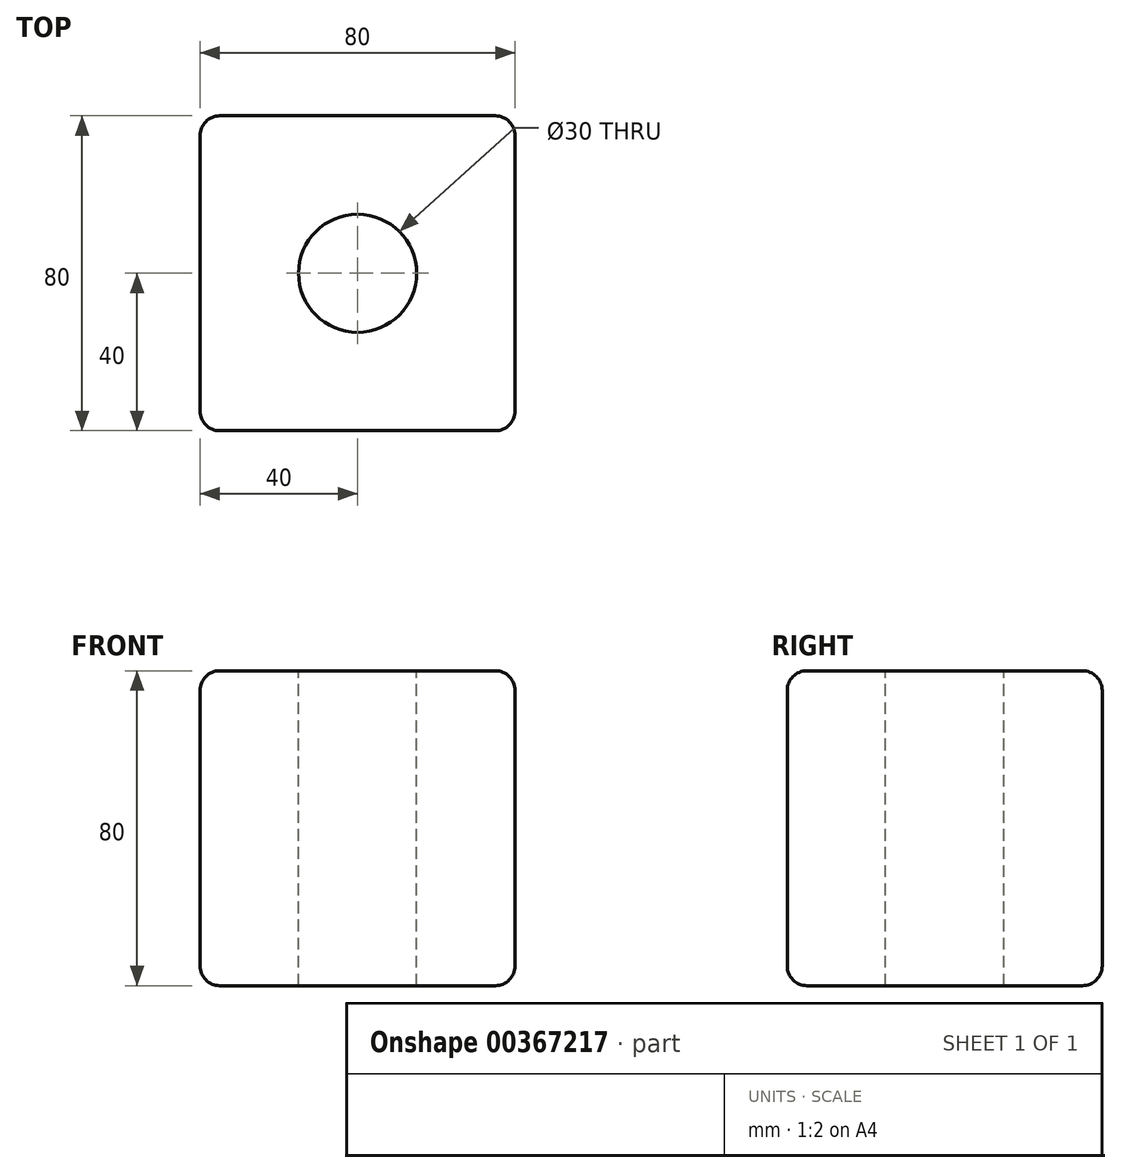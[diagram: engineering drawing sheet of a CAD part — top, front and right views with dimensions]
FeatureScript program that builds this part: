
annotation { "Feature Type Name" : "Feature", "Feature Type Description" : "" }
export const myFeature = defineFeature(function(context is Context, id is Id, definition is map)
    precondition{}
    {
        {
            var Q0;
            Q0=qCreatedBy(makeId("Top.planeOp"),FACE);
            var sketch = newSketch(context, id + "F0", { "sketchPlane" : qUnion([Q0])});
            skLineSegment(sketch, "E0.bottom", {"start": v(-94.69, 53.7) * mm, "end": v(94.69, 53.7) * mm});
            skLineSegment(sketch, "E0.top", {"start": v(-94.69, -53.7) * mm, "end": v(94.69, -53.7) * mm});
            skLineSegment(sketch, "E0.left", {"start": v(-94.69, 53.7) * mm, "end": v(-94.69, -53.7) * mm});
            skLineSegment(sketch, "E0.right", {"start": v(94.69, 53.7) * mm, "end": v(94.69, -53.7) * mm});
            skPoint(sketch, "E0.middle", {"position": v(0, 0) * mm});
            skLineSegment(sketch, "E1.bottom", {"start": v(-40, -40) * mm, "end": v(40, -40) * mm});
            skLineSegment(sketch, "E1.top", {"start": v(-40, 40) * mm, "end": v(40, 40) * mm});
            skLineSegment(sketch, "E1.left", {"start": v(-40, -40) * mm, "end": v(-40, 40) * mm});
            skLineSegment(sketch, "E1.right", {"start": v(40, -40) * mm, "end": v(40, 40) * mm});
            skSolve(sketch);
        }
        {
            var Q0;
            Q0=makeQuery(id+"F0.imprint","IMPRINT",FACE,{"disambiguationData":[TD([[makeQuery(id+"F0.imprint","IMPRINT",EDGE,{"derivedFrom":sQuery(id+"F0.wireOp",EDGE,"E1.bottom")}),1.0]])]});
            extrude(context, id + "F1", {"entities" : qUnion([Q0]), "depth" : 80 * mm});
        }
        {
            var Q0;
            Q0=makeQuery(id+"F1.opExtrude","CAP_FACE",FACE,{"disambiguationData":[OSD([sQuery(id+"F0.wireOp",EDGE,"E1.bottom"),sQuery(id+"F0.wireOp",EDGE,"E1.top"),sQuery(id+"F0.wireOp",EDGE,"E1.left"),sQuery(id+"F0.wireOp",EDGE,"E1.right")])],"isStart":false});
            var sketch = newSketch(context, id + "F2", { "sketchPlane" : qUnion([Q0])});
            skCircle(sketch, "E2", {"center": v(0, 0) * mm, "radius": 15 * mm});
            skSolve(sketch);
        }
        {
            var Q0;
            Q0=makeQuery(id+"F2.imprint","IMPRINT",FACE,{"disambiguationData":[TD([[makeQuery(id+"F2.imprint","IMPRINT",EDGE,{"derivedFrom":sQuery(id+"F2.wireOp",EDGE,"E2")}),1.0]])]});
            extrude(context, id + "F3", {"entities" : qUnion([Q0]), "operationType" : NewBodyOperationType.REMOVE, "endBound" : BoundingType.THROUGH_ALL, "oppositeDirection" : true, "depth" : 25 * mm});
        }
        {
            var Q0;
            Q0=makeQuery(id+"F1.opExtrude","SWEPT_EDGE",EDGE,{"disambiguationData":[OSD([sQuery(id+"F0.wireOp",EDGE,"E1.top"),sQuery(id+"F0.wireOp",EDGE,"E1.left")])]});
            fillet(context, id + "F4", {"entities" : qUnion([Q0]), "radius" : 5 * mm, "tangentPropagation" : true, "allowEdgeOverflow" : false});
        }
        {
            var Q0;
            Q0=makeQuery(id+"F1.opExtrude","SWEPT_EDGE",EDGE,{"disambiguationData":[OSD([sQuery(id+"F0.wireOp",EDGE,"E1.top"),sQuery(id+"F0.wireOp",EDGE,"E1.right")])]});
            fillet(context, id + "F5", {"entities" : qUnion([Q0]), "radius" : 5 * mm, "tangentPropagation" : true, "allowEdgeOverflow" : false});
        }
        {
            var Q0;
            Q0=makeQuery(id+"F1.opExtrude","CAP_EDGE",EDGE,{"disambiguationData":[OSD([sQuery(id+"F0.wireOp",EDGE,"E1.top")])],"isStart":false});
            fillet(context, id + "F6", {"entities" : qUnion([Q0]), "radius" : 5 * mm, "tangentPropagation" : true, "allowEdgeOverflow" : false});
        }
        {
            var Q0;
            Q0=makeQuery(id+"F1.opExtrude","CAP_EDGE",EDGE,{"disambiguationData":[OSD([sQuery(id+"F0.wireOp",EDGE,"E1.bottom")])],"isStart":false});
            fillet(context, id + "F7", {"entities" : qUnion([Q0]), "radius" : 5 * mm, "tangentPropagation" : true, "allowEdgeOverflow" : false});
        }
        {
            var Q0;
            Q0=makeQuery(id+"F1.opExtrude","CAP_EDGE",EDGE,{"disambiguationData":[OSD([sQuery(id+"F0.wireOp",EDGE,"E1.right")])],"isStart":true});
            fillet(context, id + "F8", {"entities" : qUnion([Q0]), "radius" : 5 * mm, "tangentPropagation" : true, "allowEdgeOverflow" : false});
        }
    });
